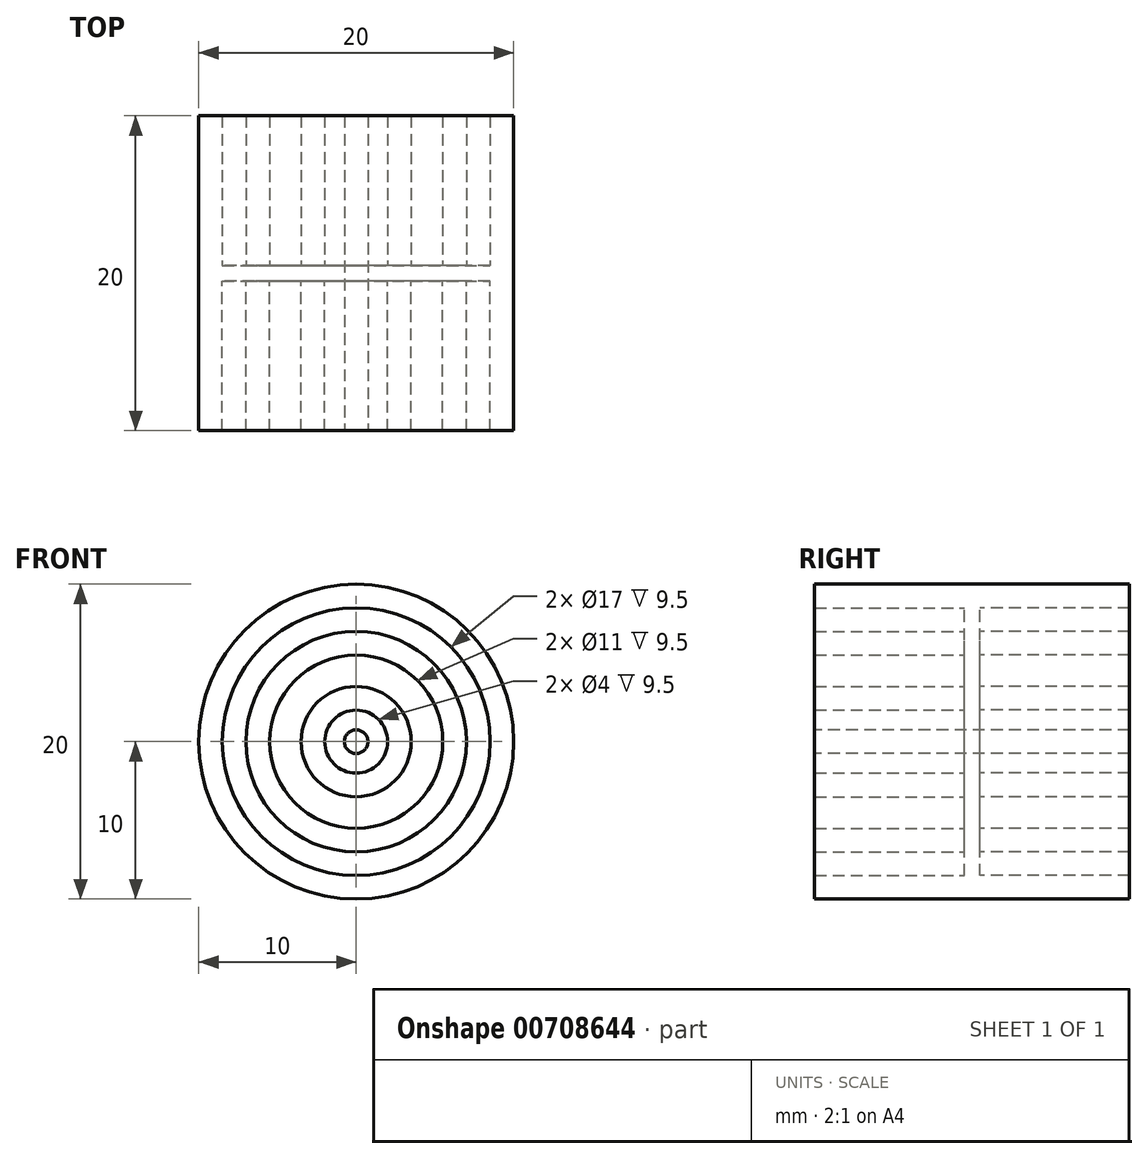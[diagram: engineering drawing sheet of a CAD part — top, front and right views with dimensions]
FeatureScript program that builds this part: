
annotation { "Feature Type Name" : "Feature", "Feature Type Description" : "" }
export const myFeature = defineFeature(function(context is Context, id is Id, definition is map)
    precondition{}
    {
        {
            var Q0;
            Q0=qCreatedBy(makeId("Front.planeOp"),FACE);
            var sketch = newSketch(context, id + "F0", { "sketchPlane" : qUnion([Q0])});
            skCircle(sketch, "E0", {"center": v(0, 0) * mm, "radius": 10 * mm});
            skCircle(sketch, "E1", {"center": v(0, 0) * mm, "radius": 8.5 * mm});
            skCircle(sketch, "E2", {"center": v(0, 0) * mm, "radius": 5.5 * mm});
            skCircle(sketch, "E3", {"center": v(0, 0) * mm, "radius": 2 * mm});
            skCircle(sketch, "E4", {"center": v(0, 0) * mm, "radius": 7 * mm});
            skCircle(sketch, "E5", {"center": v(0, 0) * mm, "radius": 3.5 * mm});
            skCircle(sketch, "E6", {"center": v(0, 0) * mm, "radius": 0.5 * mm});
            skSolve(sketch);
        }
        {
            var Q0;
            Q0=makeQuery(id+"F0.imprint","IMPRINT",FACE,{"disambiguationData":[TD([[makeQuery(id+"F0.imprint","IMPRINT",EDGE,{"derivedFrom":sQuery(id+"F0.wireOp",EDGE,"E6")}),1.0]])]});
            var sketch = newSketch(context, id + "F1", { "sketchPlane" : qUnion([Q0])});
            skCircle(sketch, "E7", {"center": v(0, 0) * mm, "radius": 10 * mm});
            skSolve(sketch);
        }
        {
            var Q0;
            Q0=qSketchRegion(id+"F1",true);
            extrude(context, id + "F2", {"entities" : qUnion([Q0]), "depth" : 1 * mm, "offsetDistance" : 25 * mm});
        }
        {
            var Q0;
            Q0=makeQuery(id+"F0.imprint","IMPRINT",FACE,{"disambiguationData":[TD([[makeQuery(id+"F0.imprint","IMPRINT",EDGE,{"derivedFrom":sQuery(id+"F0.wireOp",EDGE,"E2")}),-1.0]])]});
            var Q1;
            Q1=makeQuery(id+"F0.imprint","IMPRINT",FACE,{"disambiguationData":[TD([[makeQuery(id+"F0.imprint","IMPRINT",EDGE,{"derivedFrom":sQuery(id+"F0.wireOp",EDGE,"E3")}),-1.0]])]});
            var Q2;
            Q2=makeQuery(id+"F0.imprint","IMPRINT",FACE,{"disambiguationData":[TD([[makeQuery(id+"F0.imprint","IMPRINT",EDGE,{"derivedFrom":sQuery(id+"F0.wireOp",EDGE,"E0")}),1.0]])]});
            extrude(context, id + "F3", {"entities" : qUnion([Q0, Q1, Q2]), "operationType" : NewBodyOperationType.ADD, "depth" : 10.5 * mm, "offsetDistance" : 25 * mm});
        }
        {
            var Q0;
            Q0=qSketchRegion(id+"F0",true);
            extrude(context, id + "F4", {"entities" : qUnion([Q0]), "operationType" : NewBodyOperationType.ADD, "oppositeDirection" : true, "depth" : 9.5 * mm, "offsetDistance" : 25 * mm});
        }
        {
            var Q0;
            Q0=makeQuery(id+"F3.opExtrude","CAP_FACE",FACE,{"disambiguationData":[OSD([sQuery(id+"F0.wireOp",EDGE,"E3"),sQuery(id+"F0.wireOp",EDGE,"E5")])],"isStart":false});
            var Q1;
            Q1=makeQuery(id+"F3.opExtrude","CAP_FACE",FACE,{"disambiguationData":[OSD([sQuery(id+"F0.wireOp",EDGE,"E2"),sQuery(id+"F0.wireOp",EDGE,"E4")])],"isStart":false});
            var Q2;
            Q2=makeQuery(id+"F3.opExtrude","CAP_FACE",FACE,{"disambiguationData":[OSD([sQuery(id+"F0.wireOp",EDGE,"E0"),sQuery(id+"F0.wireOp",EDGE,"E1")])],"isStart":false});
            extrude(context, id + "F5", {"entities" : qUnion([Q0, Q1, Q2]), "operationType" : NewBodyOperationType.ADD, "oppositeDirection" : true, "depth" : 20 * mm, "offsetDistance" : 25 * mm});
        }
        {
            var Q0;
            Q0=makeQuery(id+"F3.opExtrude","CAP_FACE",FACE,{"disambiguationData":[OSD([sQuery(id+"F0.wireOp",EDGE,"E3"),sQuery(id+"F0.wireOp",EDGE,"E5")])],"isStart":false});
            var sketch = newSketch(context, id + "F6", { "sketchPlane" : qUnion([Q0])});
            skCircle(sketch, "E8", {"center": v(0, 0) * mm, "radius": 0.75 * mm});
            skSolve(sketch);
        }
        {
            var Q0;
            Q0=makeQuery(id+"F6.imprint","IMPRINT",FACE,{"disambiguationData":[TD([[makeQuery(id+"F6.imprint","IMPRINT",EDGE,{"derivedFrom":sQuery(id+"F6.wireOp",EDGE,"E8")}),1.0]])]});
            extrude(context, id + "F7", {"entities" : qUnion([Q0]), "oppositeDirection" : true, "depth" : 20 * mm, "offsetDistance" : 25 * mm});
        }
    });
